# Revit family: Sanitary_Taps-Mixers_hansgrohe_71640007-Vernis-Blend-Single-lever-showe (2)__1
name_source: partatom
category: Plumbing Fixtures
revit_build: Autodesk Revit 2015 (Build: 20140903_1530(x64)
units: mm (PartAtom-declared; Revit-internal decimal feet)

## types (1)
- Chrome 000
    BIMobject category = Taps & Mixers
    BIMobject category code = sanitary-taps-mixers
    BIMobject main category = Sanitary
    BIMobject main category code = sanitary
    Brand url = http://www.hansgrohe-int.com
    Design country = Germany
    Edition number = 1
    IFC Classification = Sanitary Terminal
    Installation instructions = https://www.hansgrohe-usa.com
    Manufacturer country = Germany
    Manufacturer name = hansgrohe
    Material main = Chrome
    Material secondary = Chrome
    Product Guid = 3bd3ee3d-8f33-4568-9870-85245f45e962
    Product SKU = 71640007
    Product data url = https://bimobject.com
    Product family = Vernis
    Product group = Pressure Balance Trim
    Product name = 71640007 Vernis Blend Single lever shower mixer for exposed installation
    Product url = https://www.hansgrohe-usa.com
    QR code = http://bimobject.com
    Technical description = https://www.hansgrohe-usa.com

## geometry (parser evidence)
native form markers: Blend x3, Sweep x3
no freeform markers — native parametric forms only
